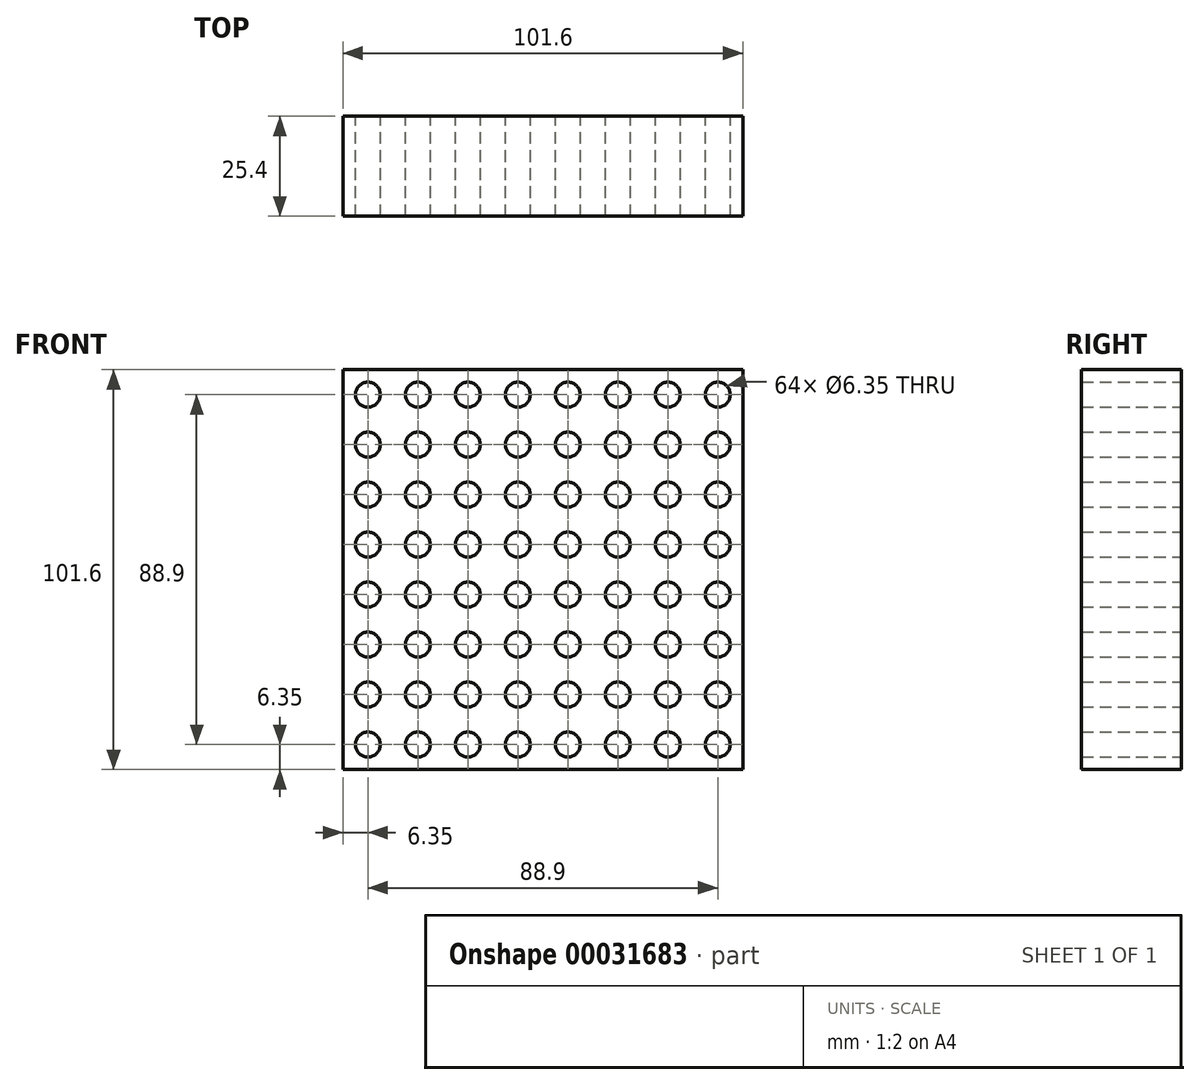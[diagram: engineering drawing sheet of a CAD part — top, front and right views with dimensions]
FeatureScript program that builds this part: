
annotation { "Feature Type Name" : "Feature", "Feature Type Description" : "" }
export const myFeature = defineFeature(function(context is Context, id is Id, definition is map)
    precondition{}
    {
        {
            var Q0;
            Q0=qCreatedBy(makeId("Front.planeOp"),FACE);
            var sketch = newSketch(context, id + "F0", { "sketchPlane" : qUnion([Q0])});
            skLineSegment(sketch, "E0.bottom", {"start": v(0, 0) * mm, "end": v(-101.6, 0) * mm});
            skLineSegment(sketch, "E0.top", {"start": v(0, 101.6) * mm, "end": v(-101.6, 101.6) * mm});
            skLineSegment(sketch, "E0.left", {"start": v(0, 0) * mm, "end": v(0, 101.6) * mm});
            skLineSegment(sketch, "E0.right", {"start": v(-101.6, 0) * mm, "end": v(-101.6, 101.6) * mm});
            skCircle(sketch, "E1", {"center": v(-95.25, 95.25) * mm, "radius": 3.18 * mm});
            skCircle(sketch, "E2.0.1.0", {"center": v(-95.25, 82.55) * mm, "radius": 3.18 * mm});
            skCircle(sketch, "E2.0.2.0", {"center": v(-95.25, 69.85) * mm, "radius": 3.18 * mm});
            skCircle(sketch, "E2.0.3.0", {"center": v(-95.25, 57.15) * mm, "radius": 3.18 * mm});
            skCircle(sketch, "E2.0.4.0", {"center": v(-95.25, 44.45) * mm, "radius": 3.18 * mm});
            skCircle(sketch, "E2.0.5.0", {"center": v(-95.25, 31.75) * mm, "radius": 3.18 * mm});
            skCircle(sketch, "E2.0.6.0", {"center": v(-95.25, 19.05) * mm, "radius": 3.18 * mm});
            skCircle(sketch, "E2.0.7.0", {"center": v(-95.25, 6.35) * mm, "radius": 3.18 * mm});
            skCircle(sketch, "E2.1.0.0", {"center": v(-82.55, 95.25) * mm, "radius": 3.18 * mm});
            skCircle(sketch, "E2.1.1.0", {"center": v(-82.55, 82.55) * mm, "radius": 3.18 * mm});
            skCircle(sketch, "E2.1.2.0", {"center": v(-82.55, 69.85) * mm, "radius": 3.18 * mm});
            skCircle(sketch, "E2.1.3.0", {"center": v(-82.55, 57.15) * mm, "radius": 3.18 * mm});
            skCircle(sketch, "E2.1.4.0", {"center": v(-82.55, 44.45) * mm, "radius": 3.18 * mm});
            skCircle(sketch, "E2.1.5.0", {"center": v(-82.55, 31.75) * mm, "radius": 3.18 * mm});
            skCircle(sketch, "E2.1.6.0", {"center": v(-82.55, 19.05) * mm, "radius": 3.18 * mm});
            skCircle(sketch, "E2.1.7.0", {"center": v(-82.55, 6.35) * mm, "radius": 3.18 * mm});
            skCircle(sketch, "E2.2.0.0", {"center": v(-69.85, 95.25) * mm, "radius": 3.18 * mm});
            skCircle(sketch, "E2.2.1.0", {"center": v(-69.85, 82.55) * mm, "radius": 3.18 * mm});
            skCircle(sketch, "E2.2.2.0", {"center": v(-69.85, 69.85) * mm, "radius": 3.18 * mm});
            skCircle(sketch, "E2.2.3.0", {"center": v(-69.85, 57.15) * mm, "radius": 3.18 * mm});
            skCircle(sketch, "E2.2.4.0", {"center": v(-69.85, 44.45) * mm, "radius": 3.18 * mm});
            skCircle(sketch, "E2.2.5.0", {"center": v(-69.85, 31.75) * mm, "radius": 3.18 * mm});
            skCircle(sketch, "E2.2.6.0", {"center": v(-69.85, 19.05) * mm, "radius": 3.18 * mm});
            skCircle(sketch, "E2.2.7.0", {"center": v(-69.85, 6.35) * mm, "radius": 3.18 * mm});
            skCircle(sketch, "E2.3.0.0", {"center": v(-57.15, 95.25) * mm, "radius": 3.18 * mm});
            skCircle(sketch, "E2.3.1.0", {"center": v(-57.15, 82.55) * mm, "radius": 3.18 * mm});
            skCircle(sketch, "E2.3.2.0", {"center": v(-57.15, 69.85) * mm, "radius": 3.18 * mm});
            skCircle(sketch, "E2.3.3.0", {"center": v(-57.15, 57.15) * mm, "radius": 3.18 * mm});
            skCircle(sketch, "E2.3.4.0", {"center": v(-57.15, 44.45) * mm, "radius": 3.18 * mm});
            skCircle(sketch, "E2.3.5.0", {"center": v(-57.15, 31.75) * mm, "radius": 3.18 * mm});
            skCircle(sketch, "E2.3.6.0", {"center": v(-57.15, 19.05) * mm, "radius": 3.18 * mm});
            skCircle(sketch, "E2.3.7.0", {"center": v(-57.15, 6.35) * mm, "radius": 3.18 * mm});
            skCircle(sketch, "E2.4.0.0", {"center": v(-44.45, 95.25) * mm, "radius": 3.18 * mm});
            skCircle(sketch, "E2.4.1.0", {"center": v(-44.45, 82.55) * mm, "radius": 3.18 * mm});
            skCircle(sketch, "E2.4.2.0", {"center": v(-44.45, 69.85) * mm, "radius": 3.18 * mm});
            skCircle(sketch, "E2.4.3.0", {"center": v(-44.45, 57.15) * mm, "radius": 3.18 * mm});
            skCircle(sketch, "E2.4.4.0", {"center": v(-44.45, 44.45) * mm, "radius": 3.18 * mm});
            skCircle(sketch, "E2.4.5.0", {"center": v(-44.45, 31.75) * mm, "radius": 3.18 * mm});
            skCircle(sketch, "E2.4.6.0", {"center": v(-44.45, 19.05) * mm, "radius": 3.18 * mm});
            skCircle(sketch, "E2.4.7.0", {"center": v(-44.45, 6.35) * mm, "radius": 3.18 * mm});
            skCircle(sketch, "E2.5.0.0", {"center": v(-31.75, 95.25) * mm, "radius": 3.18 * mm});
            skCircle(sketch, "E2.5.1.0", {"center": v(-31.75, 82.55) * mm, "radius": 3.18 * mm});
            skCircle(sketch, "E2.5.2.0", {"center": v(-31.75, 69.85) * mm, "radius": 3.18 * mm});
            skCircle(sketch, "E2.5.3.0", {"center": v(-31.75, 57.15) * mm, "radius": 3.18 * mm});
            skCircle(sketch, "E2.5.4.0", {"center": v(-31.75, 44.45) * mm, "radius": 3.18 * mm});
            skCircle(sketch, "E2.5.5.0", {"center": v(-31.75, 31.75) * mm, "radius": 3.18 * mm});
            skCircle(sketch, "E2.5.6.0", {"center": v(-31.75, 19.05) * mm, "radius": 3.18 * mm});
            skCircle(sketch, "E2.5.7.0", {"center": v(-31.75, 6.35) * mm, "radius": 3.18 * mm});
            skCircle(sketch, "E2.6.0.0", {"center": v(-19.05, 95.25) * mm, "radius": 3.18 * mm});
            skCircle(sketch, "E2.6.1.0", {"center": v(-19.05, 82.55) * mm, "radius": 3.18 * mm});
            skCircle(sketch, "E2.6.2.0", {"center": v(-19.05, 69.85) * mm, "radius": 3.18 * mm});
            skCircle(sketch, "E2.6.3.0", {"center": v(-19.05, 57.15) * mm, "radius": 3.18 * mm});
            skCircle(sketch, "E2.6.4.0", {"center": v(-19.05, 44.45) * mm, "radius": 3.18 * mm});
            skCircle(sketch, "E2.6.5.0", {"center": v(-19.05, 31.75) * mm, "radius": 3.18 * mm});
            skCircle(sketch, "E2.6.6.0", {"center": v(-19.05, 19.05) * mm, "radius": 3.18 * mm});
            skCircle(sketch, "E2.6.7.0", {"center": v(-19.05, 6.35) * mm, "radius": 3.18 * mm});
            skCircle(sketch, "E2.7.0.0", {"center": v(-6.35, 95.25) * mm, "radius": 3.18 * mm});
            skCircle(sketch, "E2.7.1.0", {"center": v(-6.35, 82.55) * mm, "radius": 3.18 * mm});
            skCircle(sketch, "E2.7.2.0", {"center": v(-6.35, 69.85) * mm, "radius": 3.18 * mm});
            skCircle(sketch, "E2.7.3.0", {"center": v(-6.35, 57.15) * mm, "radius": 3.18 * mm});
            skCircle(sketch, "E2.7.4.0", {"center": v(-6.35, 44.45) * mm, "radius": 3.18 * mm});
            skCircle(sketch, "E2.7.5.0", {"center": v(-6.35, 31.75) * mm, "radius": 3.18 * mm});
            skCircle(sketch, "E2.7.6.0", {"center": v(-6.35, 19.05) * mm, "radius": 3.18 * mm});
            skCircle(sketch, "E2.7.7.0", {"center": v(-6.35, 6.35) * mm, "radius": 3.18 * mm});
            skLineSegment(sketch, "E2.direction1", {"start": v(-95.25, 95.25) * mm, "end": v(-82.55, 95.25) * mm, "construction": true});
            skLineSegment(sketch, "E2.direction2", {"start": v(-95.25, 95.25) * mm, "end": v(-95.25, 82.55) * mm, "construction": true});
            skSolve(sketch);
        }
        {
            var Q0;
            Q0 = qSketchRegion(id + "F0", true);
            extrude(context, id + "F1", {"entities" : qUnion([Q0]), "depth" : 25.4 * mm});
        }
    });
